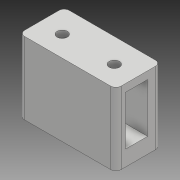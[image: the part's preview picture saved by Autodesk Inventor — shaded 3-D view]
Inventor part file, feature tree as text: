
AUTODESK INVENTOR PART (.ipt)
format: ipt  version: 2018 (Build 220112000, 112)  size: 271,872 bytes
history: native  units: mm
features: extrude x13, sketch x13, other x3, fillet x1
ambient origin geometry x8: Origin, YZ Plane, XZ Plane, XY Plane, X Axis, Y Axis, Z Axis, Center Point
bodies: Body1 (feature_tree)
feature tree (30):
  other  "Sólido1"
  extrude  "Extrusión1"  Depth=15.33mm
  extrude  "Extrusión2"  Depth=3.0mm TaperAngle=0.0deg
  extrude  "Extrusión3"  Depth=1.0mm
  extrude  "Extrusión4"  Depth=1.0mm
  extrude  "Extrusión5"  Depth=1.0mm
  extrude  "Extrusión6"  Depth=1.0mm
  extrude  "Extrusión7"  Depth=5.0mm
  extrude  "Extrusión8"  Depth=3.0mm
  extrude  "Extrusión9"  Depth=3.0mm
  extrude  "Extrusión10"  Depth=20.0mm TaperAngle=0.0deg
  extrude  "Extrusión11"  Depth=2.0mm
  fillet  "Empalme1"  Radius=3.0mm
  extrude  "Extrusión12"  Depth=12.6mm TaperAngle=0.0deg
  extrude  "Extrusión13"  Depth=3.0mm
  other  "Edición directa1"
  sketch  "Boceto1"  dims[d0=35.32mm d1=15.33mm]
  sketch  "Boceto2"  dims[d2=20.0mm d3=0.0mm d11=3.0mm d12=0.0mm]
  sketch  "Boceto3"  dims[d13=1.0mm d14=1.0mm]
  sketch  "Boceto4"  dims[d15=1.0mm d16=1.0mm]
  sketch  "Boceto5"  dims[d17=23.0mm d18=0.0mm d19=1.0mm]
  sketch  "Boceto6"  dims[d20=1.0mm d21=1.0mm]
  sketch  "Boceto7"  dims[d22=1.0mm d23=5.0mm]
  sketch  "Boceto8"  dims[d24=3.0mm d25=1.0mm]
  sketch  "Boceto9"  dims[d26=3.0mm d27=2.5mm]
  sketch  "Boceto10"  dims[d28=2.5mm d29=20.0mm d30=0.0mm]
  sketch  "Boceto11"  dims[d31=2.0mm d32=2.0mm d33=3.0mm]
  sketch  "Boceto12"  dims[d34=3.0mm d35=12.6mm d36=0.0mm]
  sketch  "Boceto13"  dims[d37=2.0mm d38=3.0mm d39=3.0mm d40=12.6mm d41=0.0mm d42=3.0mm d43=0.5mm d44=2.0mm d45=2.0mm d46=17.3mm d47=0.0mm d48=6.0mm d49=0.0mm d50=3.0mm d51=3.0mm d52=5.5mm d53=0.0mm d54=4.0mm d55=4.0mm d56=5.5mm d57=0.0mm d58=1.0mm d59=1.0mm d60=1.0mm d61=12.6mm d62=0.0mm d63=2.0mm d64=10.0mm d65=0.0mm d67=1.0mm d69=1.0mm d71=10.0mm d72=0.0mm d73=0.0mm d74=0.0mm d75=5.0mm]
  other  "Desplazar1"
